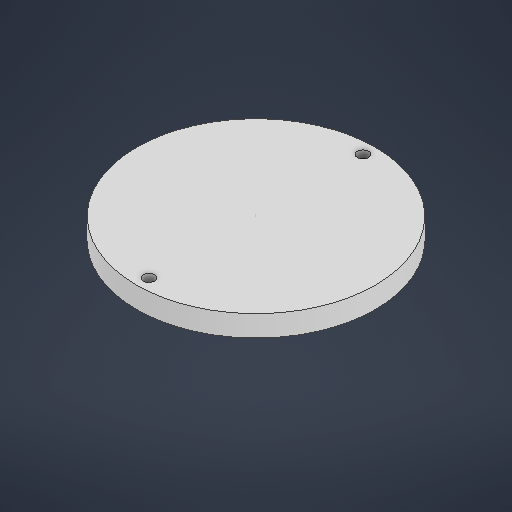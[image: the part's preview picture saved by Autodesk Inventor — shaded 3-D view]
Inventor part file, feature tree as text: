
AUTODESK INVENTOR PART (.ipt)
format: ipt  version: 2025 (Build 290162000, 162)  size: 192,512 bytes
history: native  units: in
note: dims shown in document units (in); Inventor stores cm internally (conversion verified against a paired STEP export)
features: extrude x3, sketch x2, other x1
ambient origin geometry x8: Origin, YZ Plane, XZ Plane, XY Plane, X Axis, Y Axis, Z Axis, Center Point
bodies: Solid1 (feature_tree)
feature tree (6):
  extrude  "Extrusion1"  Depth=0.5906in TaperAngle=0.0deg
  sketch  "Sketch2"  dims[d3=5.9843in d4=0.315in d5=0.315in d6=0.1772in d7=0.1772in d8=0.0in d9=0.0in d10=0.4724in d11=0.0in]
  extrude  "Extrusion2"  Depth=0.4724in
  extrude  "Extrusion3"  Depth=0.4724in
  other  "Work Axis1"
  sketch  "Sketch1"  dims[d0=6.6732in d1=0.5906in d2=0.0in]
